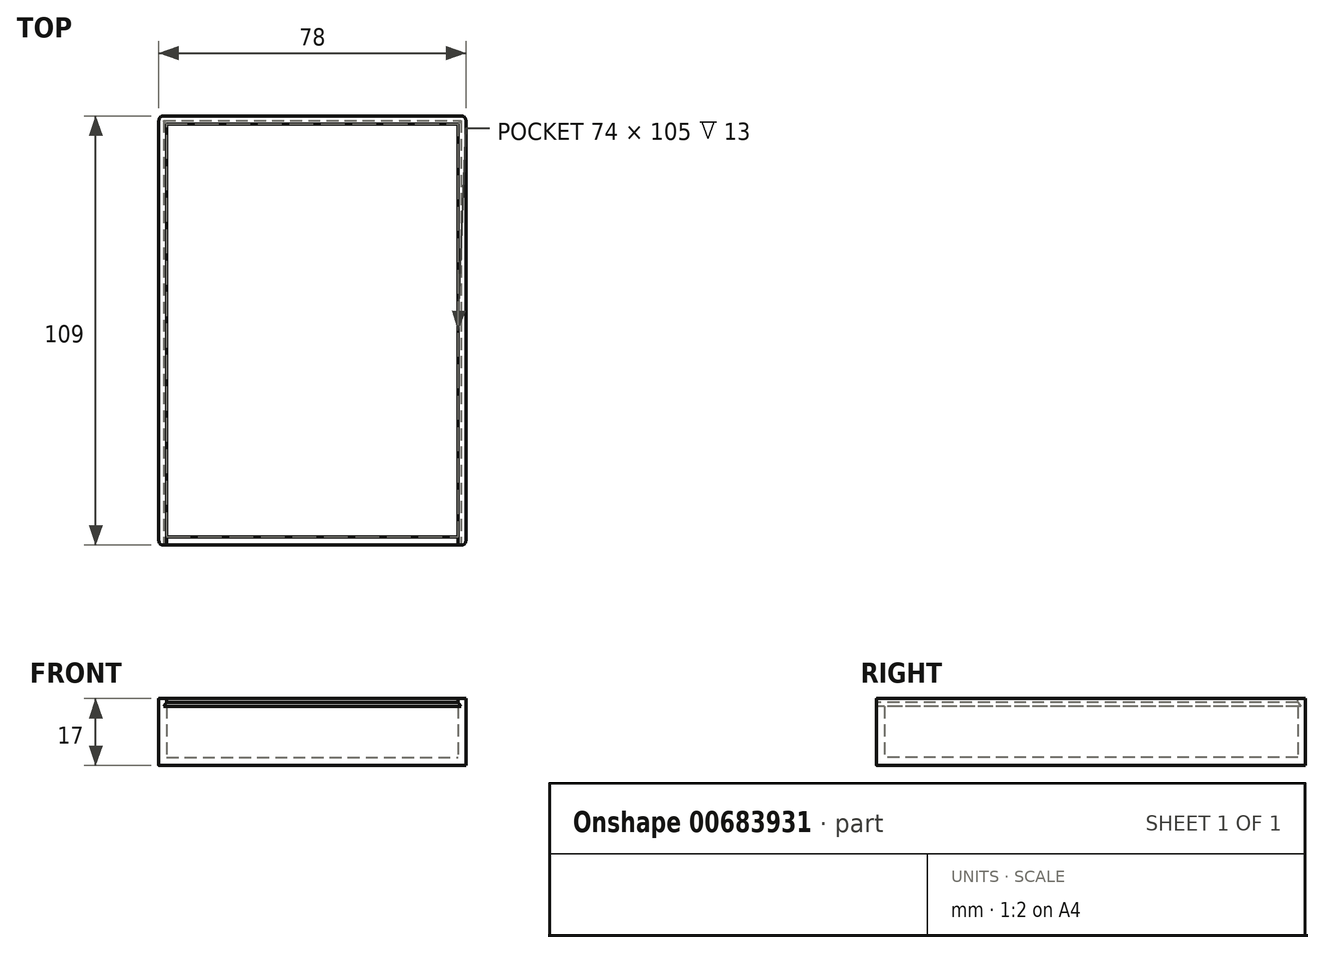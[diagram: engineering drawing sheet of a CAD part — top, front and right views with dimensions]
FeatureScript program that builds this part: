
annotation { "Feature Type Name" : "Feature", "Feature Type Description" : "" }
export const myFeature = defineFeature(function(context is Context, id is Id, definition is map)
    precondition{}
    {
        {
            var Q0;
            Q0=qCreatedBy(makeId("Front.planeOp"),FACE);
            var sketch = newSketch(context, id + "F0", { "sketchPlane" : qUnion([Q0])});
            skLineSegment(sketch, "E0.bottom", {"start": v(0, 0) * mm, "end": v(78, 0) * mm});
            skLineSegment(sketch, "E0.top", {"start": v(0, -15) * mm, "end": v(78, -15) * mm});
            skLineSegment(sketch, "E0.left", {"start": v(0, 0) * mm, "end": v(0, -15) * mm});
            skLineSegment(sketch, "E0.right", {"start": v(78, 0) * mm, "end": v(78, -15) * mm});
            skSolve(sketch);
        }
        {
            var Q0;
            Q0 = qSketchRegion(id + "F0", true);
            extrude(context, id + "F1", {"entities" : qUnion([Q0]), "oppositeDirection" : true, "depth" : 109 * mm, "offsetDistance" : 25 * mm});
        }
        {
            var Q0;
            Q0=makeQuery(id+"F1.opExtrude","SWEPT_FACE",FACE,{"disambiguationData":[OSD([sQuery(id+"F0.wireOp",EDGE,"E0.bottom")])]});
            shell(context, id + "F2", {"entities" : qUnion([Q0]), "thickness" : 2 * mm});
        }
        {
            var Q0;
            Q0=makeQuery(id+"F1.opExtrude","CAP_FACE",FACE,{"disambiguationData":[OSD([sQuery(id+"F0.wireOp",EDGE,"E0.bottom"),sQuery(id+"F0.wireOp",EDGE,"E0.top"),sQuery(id+"F0.wireOp",EDGE,"E0.left"),sQuery(id+"F0.wireOp",EDGE,"E0.right")])],"isStart":true});
            var sketch = newSketch(context, id + "F3", { "sketchPlane" : qUnion([Q0])});
            skLineSegment(sketch, "E1", {"start": v(0, 0) * mm, "end": v(0, 2) * mm});
            skLineSegment(sketch, "E2", {"start": v(0, 2) * mm, "end": v(2, 2) * mm});
            skLineSegment(sketch, "E3", {"start": v(2, 2) * mm, "end": v(2, 1) * mm});
            skLineSegment(sketch, "E4", {"start": v(1.2, 0) * mm, "end": v(0, 0) * mm});
            skLineSegment(sketch, "E5", {"start": v(39, -15) * mm, "end": v(39, 0) * mm, "construction": true});
            skLineSegment(sketch, "E6", {"start": v(1.2, 0) * mm, "end": v(2, 1) * mm});
            skLineSegment(sketch, "E7.MirrorCS", {"start": v(76.8, 0) * mm, "end": v(76, 1) * mm});
            skLineSegment(sketch, "E8.MirrorCS", {"start": v(76, 2) * mm, "end": v(76, 1) * mm});
            skLineSegment(sketch, "E9.MirrorCS", {"start": v(76.8, 0) * mm, "end": v(78, 0) * mm});
            skLineSegment(sketch, "E10.MirrorCS", {"start": v(78, 0) * mm, "end": v(78, 2) * mm});
            skLineSegment(sketch, "E11.MirrorCS", {"start": v(78, 2) * mm, "end": v(76, 2) * mm});
            skSolve(sketch);
        }
        {
            var Q0;
            Q0 = qSketchRegion(id + "F3", true);
            var Q1;
            Q1=makeQuery(id+"F1.opExtrude","CAP_FACE",FACE,{"disambiguationData":[OSD([sQuery(id+"F0.wireOp",EDGE,"E0.bottom"),sQuery(id+"F0.wireOp",EDGE,"E0.top"),sQuery(id+"F0.wireOp",EDGE,"E0.left"),sQuery(id+"F0.wireOp",EDGE,"E0.right")])],"isStart":false});
            extrude(context, id + "F4", {"entities" : qUnion([Q0]), "operationType" : NewBodyOperationType.ADD, "endBound" : BoundingType.UP_TO_SURFACE, "oppositeDirection" : true, "depth" : 25 * mm, "endBoundEntityFace" : qUnion([Q1]), "offsetDistance" : 25 * mm});
        }
        {
            var Q0;
            Q0=makeQuery(id+"F4.boolean.opBoolean","MERGE",FACE,{"derivedFrom":[makeQuery(id+"F1.opExtrude","SWEPT_FACE",FACE,{"disambiguationData":[OSD([sQuery(id+"F0.wireOp",EDGE,"E0.right")])]}),makeQuery(id+"F4.opExtrude","SWEPT_FACE",FACE,{"disambiguationData":[OSD([sQuery(id+"F3.wireOp",EDGE,"a277ad1f-f057-4d94-afe5-2e5cce70e8dc2.MirrorCS")])]})]});
            var sketch = newSketch(context, id + "F5", { "sketchPlane" : qUnion([Q0])});
            skLineSegment(sketch, "E12", {"start": v(109, 2) * mm, "end": v(107, 2) * mm});
            skLineSegment(sketch, "E13", {"start": v(109, 0) * mm, "end": v(109, 2) * mm});
            skLineSegment(sketch, "E14", {"start": v(109, 0) * mm, "end": v(107.8, 0) * mm});
            skLineSegment(sketch, "E15", {"start": v(107, 2) * mm, "end": v(107, 1) * mm});
            skLineSegment(sketch, "E16", {"start": v(107, 1) * mm, "end": v(107.8, 0) * mm});
            skSolve(sketch);
        }
        {
            var Q0;
            Q0 = qSketchRegion(id + "F5", true);
            var Q1;
            Q1=makeQuery(id+"F4.boolean.opBoolean","MERGE",FACE,{"derivedFrom":[makeQuery(id+"F1.opExtrude","SWEPT_FACE",FACE,{"disambiguationData":[OSD([sQuery(id+"F0.wireOp",EDGE,"E0.left")])]}),makeQuery(id+"F4.opExtrude","SWEPT_FACE",FACE,{"disambiguationData":[OSD([sQuery(id+"F3.wireOp",EDGE,"E1")])]})]});
            extrude(context, id + "F6", {"entities" : qUnion([Q0]), "operationType" : NewBodyOperationType.ADD, "endBound" : BoundingType.UP_TO_SURFACE, "oppositeDirection" : true, "depth" : 25 * mm, "endBoundEntityFace" : qUnion([Q1]), "offsetDistance" : 25 * mm});
        }
        {
            var Q0;
            Q0=makeQuery(id+"F4.boolean.opBoolean","MERGE",EDGE,{"derivedFrom":[makeQuery(id+"F1.opExtrude","CAP_EDGE",EDGE,{"disambiguationData":[OSD([sQuery(id+"F0.wireOp",EDGE,"E0.right")])],"isStart":true}),makeQuery(id+"F4.opExtrude","CAP_EDGE",EDGE,{"disambiguationData":[OSD([sQuery(id+"F3.wireOp",EDGE,"a277ad1f-f057-4d94-afe5-2e5cce70e8dc2.MirrorCS")])],"isStart":true})]});
            var Q1;
            {var subQ0=sQuery(id+"F0.wireOp",EDGE,"E0.right");Q1=makeQuery(id+"F4.boolean.opBoolean","MERGE",EDGE,{"derivedFrom":[makeQuery(id+"F1.opExtrude","CAP_EDGE",EDGE,{"disambiguationData":[OSD([subQ0])],"isStart":false}),makeQuery(id+"F4.opExtrude","TWEAK_EDGE",EDGE,{"derivedFrom":[makeQuery(id+"F1.opExtrude","CAP_FACE",FACE,{"disambiguationData":[OSD([sQuery(id+"F0.wireOp",EDGE,"E0.bottom"),sQuery(id+"F0.wireOp",EDGE,"E0.top"),sQuery(id+"F0.wireOp",EDGE,"E0.left"),subQ0])],"isStart":false}),makeQuery(id+"F3.imprint","IMPRINT",EDGE,{"derivedFrom":sQuery(id+"F3.wireOp",EDGE,"a277ad1f-f057-4d94-afe5-2e5cce70e8dc2.MirrorCS")})]})]});}
            var Q2;
            {var subQ0=sQuery(id+"F0.wireOp",EDGE,"E0.left");Q2=makeQuery(id+"F4.boolean.opBoolean","MERGE",EDGE,{"derivedFrom":[makeQuery(id+"F1.opExtrude","CAP_EDGE",EDGE,{"disambiguationData":[OSD([subQ0])],"isStart":false}),makeQuery(id+"F4.opExtrude","TWEAK_EDGE",EDGE,{"derivedFrom":[makeQuery(id+"F1.opExtrude","CAP_FACE",FACE,{"disambiguationData":[OSD([sQuery(id+"F0.wireOp",EDGE,"E0.bottom"),sQuery(id+"F0.wireOp",EDGE,"E0.top"),subQ0,sQuery(id+"F0.wireOp",EDGE,"E0.right")])],"isStart":false}),makeQuery(id+"F3.imprint","IMPRINT",EDGE,{"derivedFrom":sQuery(id+"F3.wireOp",EDGE,"E1")})]})]});}
            var Q3;
            Q3=makeQuery(id+"F4.boolean.opBoolean","MERGE",EDGE,{"derivedFrom":[makeQuery(id+"F1.opExtrude","CAP_EDGE",EDGE,{"disambiguationData":[OSD([sQuery(id+"F0.wireOp",EDGE,"E0.left")])],"isStart":true}),makeQuery(id+"F4.opExtrude","CAP_EDGE",EDGE,{"disambiguationData":[OSD([sQuery(id+"F3.wireOp",EDGE,"E1")])],"isStart":true})]});
            fillet(context, id + "F7", {"entities" : qUnion([Q0, Q1, Q2, Q3]), "radius" : 1.2 * mm, "tangentPropagation" : true, "rho" : 0.5, "crossSection" : FilletCrossSection.CONIC, "allowEdgeOverflow" : false});
        }
    });
